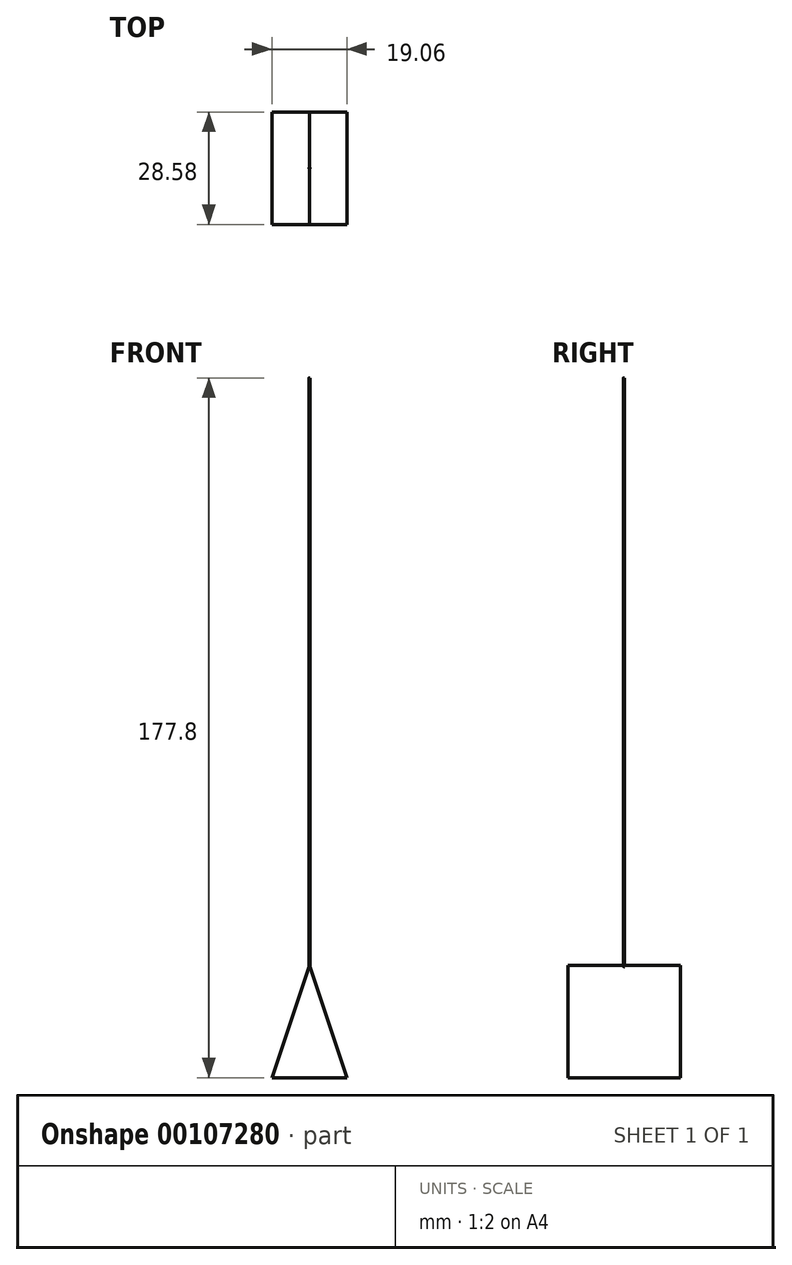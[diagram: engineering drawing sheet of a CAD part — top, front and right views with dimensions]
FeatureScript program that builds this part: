
annotation { "Feature Type Name" : "Feature", "Feature Type Description" : "" }
export const myFeature = defineFeature(function(context is Context, id is Id, definition is map)
    precondition{}
    {
        {
            var Q0;
            Q0=qCreatedBy(makeId("Front.planeOp"),FACE);
            var sketch = newSketch(context, id + "F0", { "sketchPlane" : qUnion([Q0])});
            skLineSegment(sketch, "E0.0", {"start": v(-9.53, 0) * mm, "end": v(0, 28.58) * mm});
            skLineSegment(sketch, "E0.1", {"start": v(0, 28.58) * mm, "end": v(9.52, 0) * mm});
            skLineSegment(sketch, "E0.2", {"start": v(9.52, 0) * mm, "end": v(-9.53, 0) * mm});
            skPoint(sketch, "E0.0.midPoint", {"position": v(-4.76, 14.29) * mm});
            skSolve(sketch);
        }
        {
            var Q0;
            Q0=makeQuery(id+"F0.imprint","IMPRINT",FACE,{"disambiguationData":[TD([[makeQuery(id+"F0.imprint","IMPRINT",EDGE,{"derivedFrom":sQuery(id+"F0.wireOp",EDGE,"E0.0")}),-1.0]])]});
            extrude(context, id + "F1", {"entities" : qUnion([Q0]), "endBound" : BoundingType.SYMMETRIC, "depth" : 28.57 * mm});
        }
        {
            var Q0;
            Q0=qCreatedBy(makeId("Top.planeOp"),FACE);
            var sketch = newSketch(context, id + "F2", { "sketchPlane" : qUnion([Q0])});
            skCircle(sketch, "E1", {"center": v(0, 0) * mm, "radius": 0.16 * mm});
            skSolve(sketch);
        }
        {
            var Q0;
            Q0=qSketchRegion(id+"F2",true);
            extrude(context, id + "F3", {"entities" : qUnion([Q0]), "operationType" : NewBodyOperationType.ADD, "depth" : 177.8 * mm});
        }
    });
